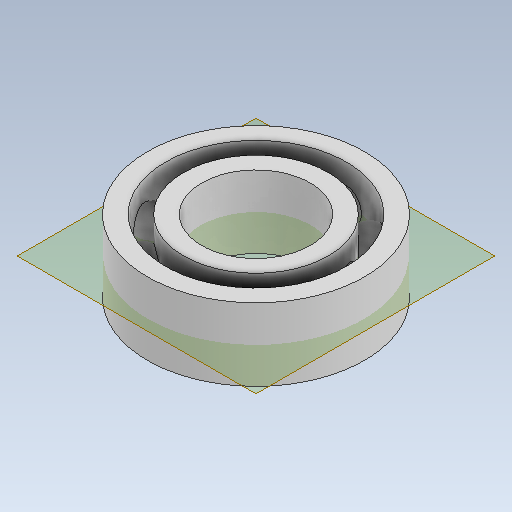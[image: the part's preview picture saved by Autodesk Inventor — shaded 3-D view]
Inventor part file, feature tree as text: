
AUTODESK INVENTOR PART (.ipt)
format: ipt  version: 2023 (Build 270158000, 158)  size: 228,864 bytes
history: native  units: mm
features: sketch x3, extrude x2, plane x1, revolve x1, pattern_circular x1, projected_geometry x1
ambient origin geometry x8: Origin, YZ Plane, XZ Plane, XY Plane, X Axis, Y Axis, Z Axis, Center Point
bodies: Solid1 (feature_tree)
feature tree (9):
  extrude  "Extrusion1"  Depth=3.0mm
  extrude  "Extrusion2"  Depth=4.0mm
  plane  "Work Plane1"
  revolve  "Revolution1"  [1 undecoded]
  pattern_circular  "Circular Pattern1"  [2 undecoded]
  sketch  "Sketch1"  dims[d0=6.0mm d1=3.0mm]
  sketch  "Sketch2"  dims[d2=2.0mm d3=0.0mm d4=4.0mm]
  projected_geometry  "Projected Loop1"
  sketch  "Sketch3"  dims[d5=5.0mm d6=2.0mm d7=0.0mm d8=1.0mm d9=90.0deg d10=100.0mm d11=360.0deg]
note: 3 required parameter values undecoded (feature->parameter linkage not recoverable at this tier; creation-order binding heuristic only, values carry confidence <= 0.55)